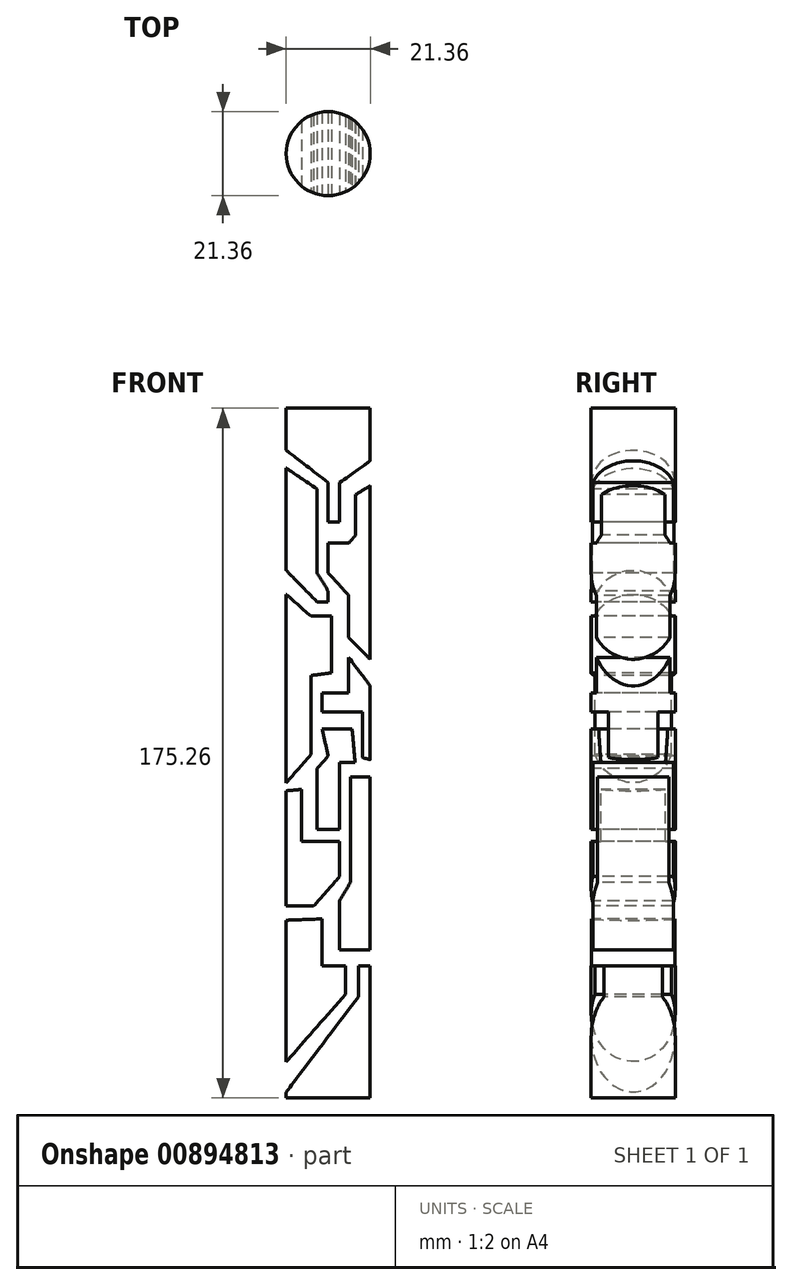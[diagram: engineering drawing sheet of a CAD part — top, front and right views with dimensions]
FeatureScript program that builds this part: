
annotation { "Feature Type Name" : "Feature", "Feature Type Description" : "" }
export const myFeature = defineFeature(function(context is Context, id is Id, definition is map)
    precondition{}
    {
        {
            var Q0;
            Q0=qCreatedBy(makeId("Top.planeOp"),FACE);
            var sketch = newSketch(context, id + "F0", { "sketchPlane" : qUnion([Q0])});
            skCircle(sketch, "E0", {"center": v(0, 0) * mm, "radius": 10.68 * mm});
            skSolve(sketch);
        }
        {
            var Q0;
            Q0=makeQuery(id+"F0.imprint","IMPRINT",FACE,{"disambiguationData":[TD([[makeQuery(id+"F0.imprint","IMPRINT",EDGE,{"derivedFrom":sQuery(id+"F0.wireOp",EDGE,"E0")}),1.0]])]});
            extrude(context, id + "F1", {"entities" : qUnion([Q0]), "oppositeDirection" : true, "depth" : 137.16 * mm, "offsetDistance" : 25.4 * mm});
        }
        {
            var Q0;
            Q0=makeQuery(id+"F1.opExtrude","CAP_FACE",FACE,{"disambiguationData":[OSD([sQuery(id+"F0.wireOp",EDGE,"E0")])],"isStart":true});
            extrude(context, id + "F2", {"entities" : qUnion([Q0]), "operationType" : NewBodyOperationType.ADD, "depth" : 38.1 * mm, "offsetDistance" : 25.4 * mm});
        }
        {
            var Q0;
            Q0=qCreatedBy(makeId("Front.planeOp"),FACE);
            var sketch = newSketch(context, id + "F3", { "sketchPlane" : qUnion([Q0])});
            skLineSegment(sketch, "E1", {"start": v(11.9, 25.61) * mm, "end": v(2.92, 19.17) * mm});
            skLineSegment(sketch, "E2", {"start": v(2.92, 19.17) * mm, "end": v(2.92, 9.17) * mm});
            skLineSegment(sketch, "E3", {"start": v(2.92, 9.17) * mm, "end": v(0, 9.17) * mm});
            skLineSegment(sketch, "E4", {"start": v(0, 9.17) * mm, "end": v(0, 19.17) * mm});
            skLineSegment(sketch, "E5", {"start": v(0, 19.17) * mm, "end": v(-17.06, 32.37) * mm});
            skLineSegment(sketch, "E6", {"start": v(-17.06, 32.37) * mm, "end": v(-15.32, 26.02) * mm});
            skLineSegment(sketch, "E7", {"start": v(-15.32, 26.02) * mm, "end": v(-2.82, 17.56) * mm});
            skLineSegment(sketch, "E8", {"start": v(-2.82, 17.56) * mm, "end": v(-2.82, -3.79) * mm});
            skLineSegment(sketch, "E9", {"start": v(-2.82, -3.79) * mm, "end": v(0, -8.4) * mm});
            skLineSegment(sketch, "E10", {"start": v(0, -8.4) * mm, "end": v(0, -11.1) * mm});
            skLineSegment(sketch, "E11", {"start": v(0, -11.1) * mm, "end": v(-2.82, -11.1) * mm});
            skLineSegment(sketch, "E12", {"start": v(-2.82, -11.1) * mm, "end": v(-13.79, 0) * mm});
            skLineSegment(sketch, "E13", {"start": v(-13.79, 0) * mm, "end": v(-17.06, -8.4) * mm});
            skLineSegment(sketch, "E14", {"start": v(-17.06, -8.4) * mm, "end": v(-13.98, -6.29) * mm});
            skLineSegment(sketch, "E15", {"start": v(-13.98, -6.29) * mm, "end": v(-4.4, -14.73) * mm});
            skLineSegment(sketch, "E16", {"start": v(-4.4, -14.73) * mm, "end": v(0.87, -14.73) * mm});
            skLineSegment(sketch, "E17", {"start": v(0.87, -14.73) * mm, "end": v(0.87, -29.14) * mm});
            skLineSegment(sketch, "E18", {"start": v(0.87, -29.14) * mm, "end": v(-4.4, -29.83) * mm});
            skLineSegment(sketch, "E19", {"start": v(-4.4, -29.83) * mm, "end": v(-4.4, -49.94) * mm});
            skLineSegment(sketch, "E20", {"start": v(-4.4, -49.94) * mm, "end": v(-12.61, -59.27) * mm});
            skLineSegment(sketch, "E21", {"start": v(-12.61, -59.27) * mm, "end": v(-6.85, -58.77) * mm});
            skLineSegment(sketch, "E22", {"start": v(-6.85, -58.77) * mm, "end": v(-6.85, -71.97) * mm});
            skLineSegment(sketch, "E23", {"start": v(-6.85, -71.97) * mm, "end": v(2.92, -71.97) * mm});
            skLineSegment(sketch, "E24", {"start": v(2.92, -71.97) * mm, "end": v(2.92, -80.9) * mm});
            skLineSegment(sketch, "E25", {"start": v(2.92, -80.9) * mm, "end": v(-3.68, -88.4) * mm});
            skLineSegment(sketch, "E26", {"start": v(-3.68, -88.4) * mm, "end": v(-13.98, -88.4) * mm});
            skLineSegment(sketch, "E27", {"start": v(-13.98, -88.4) * mm, "end": v(-13.66, -92.11) * mm});
            skLineSegment(sketch, "E28", {"start": v(-13.66, -92.11) * mm, "end": v(-1.57, -91.66) * mm});
            skLineSegment(sketch, "E29", {"start": v(-1.57, -91.66) * mm, "end": v(-1.57, -103.58) * mm});
            skLineSegment(sketch, "E30", {"start": v(-1.57, -103.58) * mm, "end": v(4.43, -103.58) * mm});
            skLineSegment(sketch, "E31", {"start": v(4.43, -103.58) * mm, "end": v(4.43, -110.8) * mm});
            skLineSegment(sketch, "E32", {"start": v(4.43, -110.8) * mm, "end": v(-17.06, -135.21) * mm});
            skLineSegment(sketch, "E33", {"start": v(-17.06, -135.21) * mm, "end": v(-13.98, -140.04) * mm});
            skLineSegment(sketch, "E34", {"start": v(-13.98, -140.04) * mm, "end": v(7.65, -111.46) * mm});
            skLineSegment(sketch, "E35", {"start": v(7.65, -111.46) * mm, "end": v(7.65, -103.55) * mm});
            skLineSegment(sketch, "E36", {"start": v(7.65, -103.55) * mm, "end": v(17.08, -103.55) * mm});
            skLineSegment(sketch, "E37", {"start": v(17.08, -103.55) * mm, "end": v(16.74, -99.54) * mm});
            skLineSegment(sketch, "E38", {"start": v(16.74, -99.54) * mm, "end": v(2.92, -99.54) * mm});
            skLineSegment(sketch, "E39", {"start": v(2.92, -99.54) * mm, "end": v(2.92, -87.05) * mm});
            skLineSegment(sketch, "E40", {"start": v(2.92, -87.05) * mm, "end": v(5.66, -82.35) * mm});
            skLineSegment(sketch, "E41", {"start": v(5.66, -82.35) * mm, "end": v(5.66, -55.57) * mm});
            skLineSegment(sketch, "E42", {"start": v(5.66, -55.57) * mm, "end": v(13.82, -55.57) * mm});
            skLineSegment(sketch, "E43", {"start": v(13.82, -55.57) * mm, "end": v(13.82, -51.96) * mm});
            skLineSegment(sketch, "E44", {"start": v(13.82, -51.96) * mm, "end": v(8.65, -50.68) * mm});
            skLineSegment(sketch, "E45", {"start": v(8.65, -50.68) * mm, "end": v(8.65, -39.09) * mm});
            skLineSegment(sketch, "E46", {"start": v(8.65, -39.09) * mm, "end": v(-1.57, -39.09) * mm});
            skLineSegment(sketch, "E47", {"start": v(-1.57, -39.09) * mm, "end": v(-1.57, -34.31) * mm});
            skLineSegment(sketch, "E48", {"start": v(-1.57, -34.31) * mm, "end": v(5.18, -34.31) * mm});
            skLineSegment(sketch, "E49", {"start": v(5.18, -34.31) * mm, "end": v(5.18, -25.21) * mm});
            skLineSegment(sketch, "E50", {"start": v(5.18, -25.21) * mm, "end": v(12.16, -34.44) * mm});
            skLineSegment(sketch, "E51", {"start": v(12.16, -34.44) * mm, "end": v(15.51, -30.63) * mm});
            skLineSegment(sketch, "E52", {"start": v(15.51, -30.63) * mm, "end": v(5.2, -20.2) * mm});
            skLineSegment(sketch, "E53", {"start": v(5.2, -20.2) * mm, "end": v(5.2, -9.48) * mm});
            skLineSegment(sketch, "E54", {"start": v(5.2, -9.48) * mm, "end": v(0, -3.79) * mm});
            skLineSegment(sketch, "E55", {"start": v(0, -3.79) * mm, "end": v(0, 3.9) * mm});
            skLineSegment(sketch, "E56", {"start": v(0, 3.9) * mm, "end": v(5.3, 3.9) * mm});
            skLineSegment(sketch, "E57", {"start": v(5.3, 3.9) * mm, "end": v(6.98, 5.82) * mm});
            skLineSegment(sketch, "E58", {"start": v(6.98, 5.82) * mm, "end": v(6.98, 16.13) * mm});
            skLineSegment(sketch, "E59", {"start": v(6.98, 16.13) * mm, "end": v(15.74, 21.56) * mm});
            skLineSegment(sketch, "E60", {"start": v(15.74, 21.56) * mm, "end": v(11.9, 25.61) * mm});
            skLineSegment(sketch, "E61", {"start": v(-1.57, -43.35) * mm, "end": v(6.07, -43.35) * mm});
            skLineSegment(sketch, "E62", {"start": v(6.07, -43.35) * mm, "end": v(6.8, -51.88) * mm});
            skLineSegment(sketch, "E63", {"start": v(6.8, -51.88) * mm, "end": v(2.92, -51.88) * mm});
            skLineSegment(sketch, "E64", {"start": v(2.92, -51.88) * mm, "end": v(2.92, -68.98) * mm});
            skLineSegment(sketch, "E65", {"start": v(2.92, -68.98) * mm, "end": v(-2.82, -68.98) * mm});
            skLineSegment(sketch, "E66", {"start": v(-2.82, -68.98) * mm, "end": v(-2.82, -53.44) * mm});
            skLineSegment(sketch, "E67", {"start": v(-2.82, -53.44) * mm, "end": v(0, -50.24) * mm});
            skLineSegment(sketch, "E68", {"start": v(0, -50.24) * mm, "end": v(-1.57, -43.35) * mm});
            skLineSegment(sketch, "E69.bottom", {"start": v(-36.44, 47.03) * mm, "end": v(37.41, 47.03) * mm});
            skLineSegment(sketch, "E69.top", {"start": v(-36.44, -157.6) * mm, "end": v(37.41, -157.6) * mm});
            skLineSegment(sketch, "E69.left", {"start": v(-36.44, 47.03) * mm, "end": v(-36.44, -157.6) * mm});
            skLineSegment(sketch, "E69.right", {"start": v(37.41, 47.03) * mm, "end": v(37.41, -157.6) * mm});
            skSolve(sketch);
        }
        {
            var Q0;
            Q0=makeQuery(id+"F3.imprint","IMPRINT",FACE,{"disambiguationData":[TD([[makeQuery(id+"F3.imprint","IMPRINT",EDGE,{"derivedFrom":sQuery(id+"F3.wireOp",EDGE,"E1")}),1.0]])]});
            extrude(context, id + "F4", {"entities" : qUnion([Q0]), "operationType" : NewBodyOperationType.REMOVE, "oppositeDirection" : true, "depth" : 35.56 * mm, "offsetDistance" : 25.4 * mm, "symmetric" : true});
        }
    });
